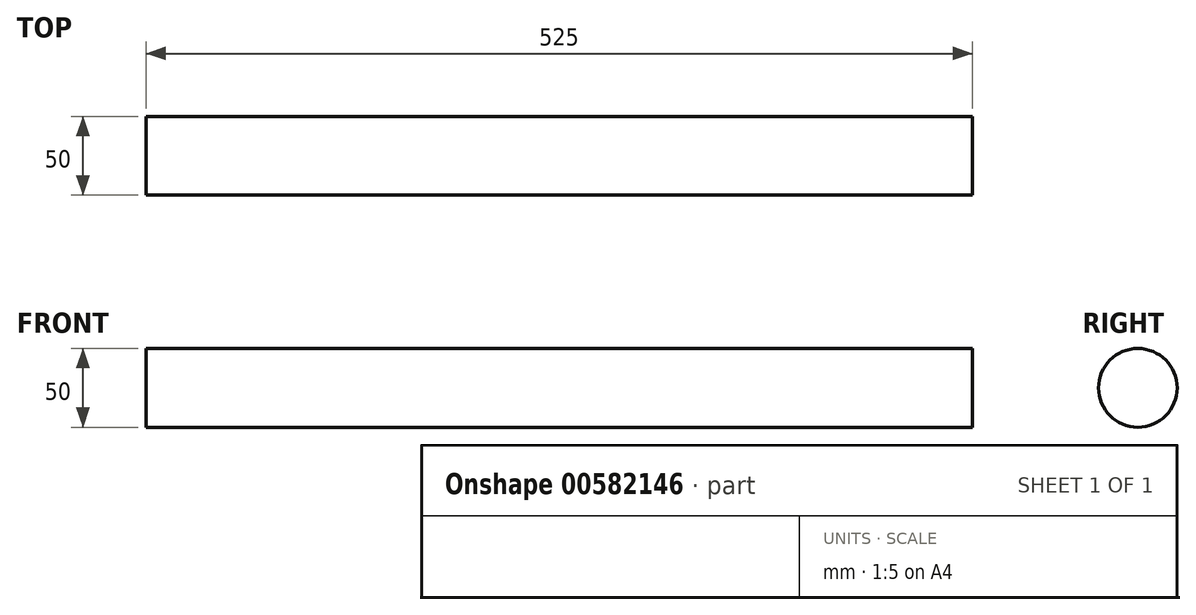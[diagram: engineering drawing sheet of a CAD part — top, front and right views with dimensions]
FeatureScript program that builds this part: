
annotation { "Feature Type Name" : "Feature", "Feature Type Description" : "" }
export const myFeature = defineFeature(function(context is Context, id is Id, definition is map)
    precondition{}
    {
        {
            var Q0;
            Q0=qCreatedBy(makeId("Right.planeOp"),FACE);
            var sketch = newSketch(context, id + "F0", { "sketchPlane" : qUnion([Q0])});
            skCircle(sketch, "E0", {"center": v(0, 0) * mm, "radius": 25 * mm});
            skSolve(sketch);
        }
        {
            var Q0;
            Q0 = qSketchRegion(id + "F0", true);
            extrude(context, id + "F1", {"entities" : qUnion([Q0]), "depth" : 525 * mm, "offsetDistance" : 25 * mm});
        }
    });
